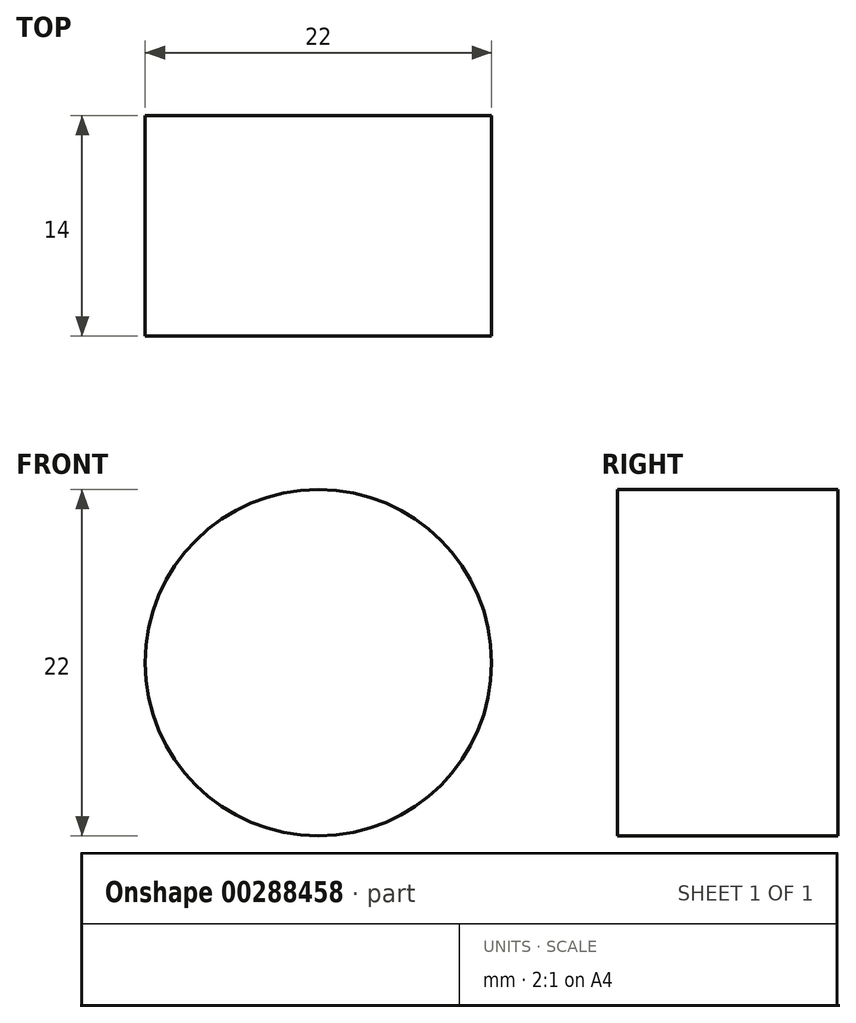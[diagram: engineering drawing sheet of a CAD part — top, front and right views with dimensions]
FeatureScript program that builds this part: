
annotation { "Feature Type Name" : "Feature", "Feature Type Description" : "" }
export const myFeature = defineFeature(function(context is Context, id is Id, definition is map)
    precondition{}
    {
        {
            var Q0;
            Q0=qCreatedBy(makeId("Front.planeOp"),FACE);
            var sketch = newSketch(context, id + "F0", { "sketchPlane" : qUnion([Q0])});
            skCircle(sketch, "E0", {"center": v(0, 0) * mm, "radius": 11 * mm});
            skSolve(sketch);
        }
        {
            var Q0;
            {var subQ5=sQuery(id+"F0.wireOp",EDGE,"QYFrYans-syh9-8i3C-TEEM-U4O6hzT8mJtS.right");Q0=makeQuery(id+"F0.imprint","IMPRINT",FACE,{"disambiguationData":[TD([[makeQuery(id+"F0.imprint","IMPRINT",EDGE,{"derivedFrom":subQ5}),-1.0]])]});}
            var Q1;
            {var subQ5=sQuery(id+"F0.wireOp",EDGE,"QYFrYans-syh9-8i3C-TEEM-U4O6hzT8mJtS.right");Q1=makeQuery(id+"F0.imprint","IMPRINT",FACE,{"disambiguationData":[TD([[makeQuery(id+"F0.imprint","IMPRINT",EDGE,{"derivedFrom":subQ5}),1.0]])]});}
            var Q2;
            Q2=makeQuery(id+"F0.imprint","IMPRINT",FACE,{"disambiguationData":[TD([[makeQuery(id+"F0.imprint","IMPRINT",EDGE,{"derivedFrom":sQuery(id+"F0.wireOp",EDGE,"E0")}),1.0]])]});
            extrude(context, id + "F1", {"entities" : qUnion([Q0, Q1, Q2]), "oppositeDirection" : true, "depth" : 14 * mm});
        }
    });
